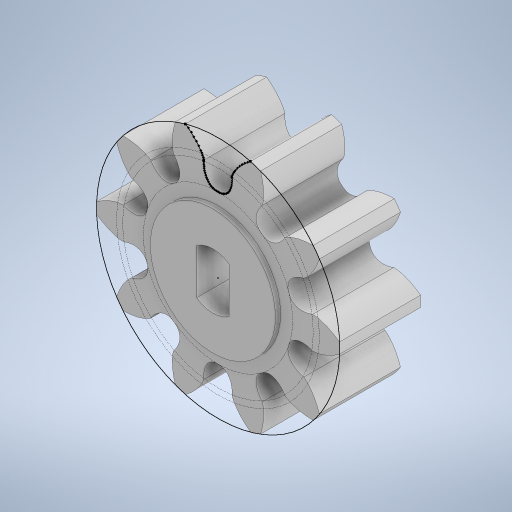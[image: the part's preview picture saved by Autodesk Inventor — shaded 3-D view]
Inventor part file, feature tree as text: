
AUTODESK INVENTOR PART (.ipt)
format: ipt  version: 2023 (Build 270158000, 158)  size: 444,416 bytes
history: native  units: mm
features: extrude x4, sketch x3, pattern_circular x1, projected_geometry x1
ambient origin geometry x8: Origin, YZ Plane, XZ Plane, XY Plane, X Axis, Y Axis, Z Axis, Center Point
bodies: Solid1 (feature_tree)
feature tree (9):
  sketch  "Sketch1"  dims[d0=8.0mm d1=0.0mm]
  extrude  "Extrusion1"  TaperAngle=0.0deg  [1 undecoded]
  extrude  "Extrusion2"  Depth=10.0mm TaperAngle=360.0deg
  pattern_circular  "Circular Pattern1"  [2 undecoded]
  extrude  "Extrusion3"  Depth=10.0mm TaperAngle=0.0deg
  extrude  "Extrusion4"  Depth=0.5mm TaperAngle=0.0deg
  sketch  "Sketch2"  dims[d2=10.0mm d3=0.0mm d4=100.0mm d5=360.0deg]
  sketch  "Sketch3"  dims[d7=5.5mm d10=3.2mm d11=10.0mm d12=0.0mm d13=0.5mm d14=0.0mm]
  projected_geometry  "Projected Loop1"
note: 3 required parameter values undecoded (feature->parameter linkage not recoverable at this tier; creation-order binding heuristic only, values carry confidence <= 0.55)
